# Revit family: BE_33529_de_DE
name_source: partatom
category: Leuchten
revit_build: Autodesk Revit 2015 (Build: 20151008_0715(x64)
units: mm (PartAtom-declared; Revit-internal decimal feet)

## types (6) — shared parameters
AC/DC = AC/DC
Aktualisierung = 2015-10-29T04:09:10
BEGA_Dummy = Nein
BEGA_IES = Ja
BEGA_Intern = Ja
BEGA_Intern_Konstruktion = Ja
BEGA_Intern_an = Ja
BEGA_Intern_aus = Ja
Befestigungsabstand = 195 mm
Befestigungsbohrung = Ø 5 mm
Beschreibung = Wandleuchte
Beschreibung_Sonderanfertigung = Hier können Sie Informationen zur Sonderanfertigung eintragen.
CE_Konformität = ja
Energieeffizienzklasse = LED A++ - A
Farbfilter = 16777215
Farbtemperaturverschiebung bei Dämpfen der Lampe = <Keine Auswahl>
Farbwiedergabeindex = Ra > 80
Frequenz = 0/50-60 Hz
Gewicht = 2.6 kg
Hersteller = BEGA
Lampe = LED 6.3 W
Lastklassifizierung = Beleuchtung
Lebensdauerkriterien = L70 = 50.000 h
Leuchtenlichtstrom = 284 lm
Logo = BEGA_Logo.png
Material_02 = BEGA_Oberfläche_Silber_matt
Material_03 = BEGA_Oberfläche_Weiss_matt
Material_06 = BEGA_Oberfläche_Edelstahl_gebürstet
Material_11 = BEGA_Glas_opal
Neigungswinkel = 0.00°
Produktdatenblatt = http://www.bega.de
Scheinlast = 0 VA
Schutzart = IP 65
Schutzklasse = I
Sonderanfertigung = Nein
Spannung = 0 V
Typenbild = 33529.png
URL = http://www.bega.de
zero-valued in all types: Vorgabe-Ansicht

## per-type parameters (varying)
| type | Bestellnummer | Datei für fotometrisches Netz | Farbtemperatur | LED_Modulbezeichnung | Lampenlichtstrom | M_A | M_G | M_W | Modell |
| BEGA_33529_Weiß_K3 | 33529W | BE_33529.IES | 3000 K | LED-0263/830 | 735 lm | Nein | Nein | Ja | 33529W |
| BEGA_33529_Grafit_K4 | 33529K4 | BE_33529K4.IES | 4000 K | LED-0263/840 | 790 lm | Nein | Ja | Nein | 33529K4 |
| BEGA_33529_Silber_K4 | 33529AK4 | BE_33529K4.IES | 4000 K | LED-0263/840 | 790 lm | Ja | Nein | Nein | 33529AK4 |
| BEGA_33529_Silber_K3 | 33529A | BE_33529.IES | 3000 K | LED-0263/830 | 735 lm | Ja | Nein | Nein | 33529A |
| BEGA_33529_Grafit_K3 | 33529 | BE_33529.IES | 3000 K | LED-0263/830 | 735 lm | Nein | Ja | Nein | 33529 |
| BEGA_33529_Weiß_K4 | 33529WK4 | BE_33529K4.IES | 4000 K | LED-0263/840 | 790 lm | Nein | Nein | Ja | 33529WK4 |
